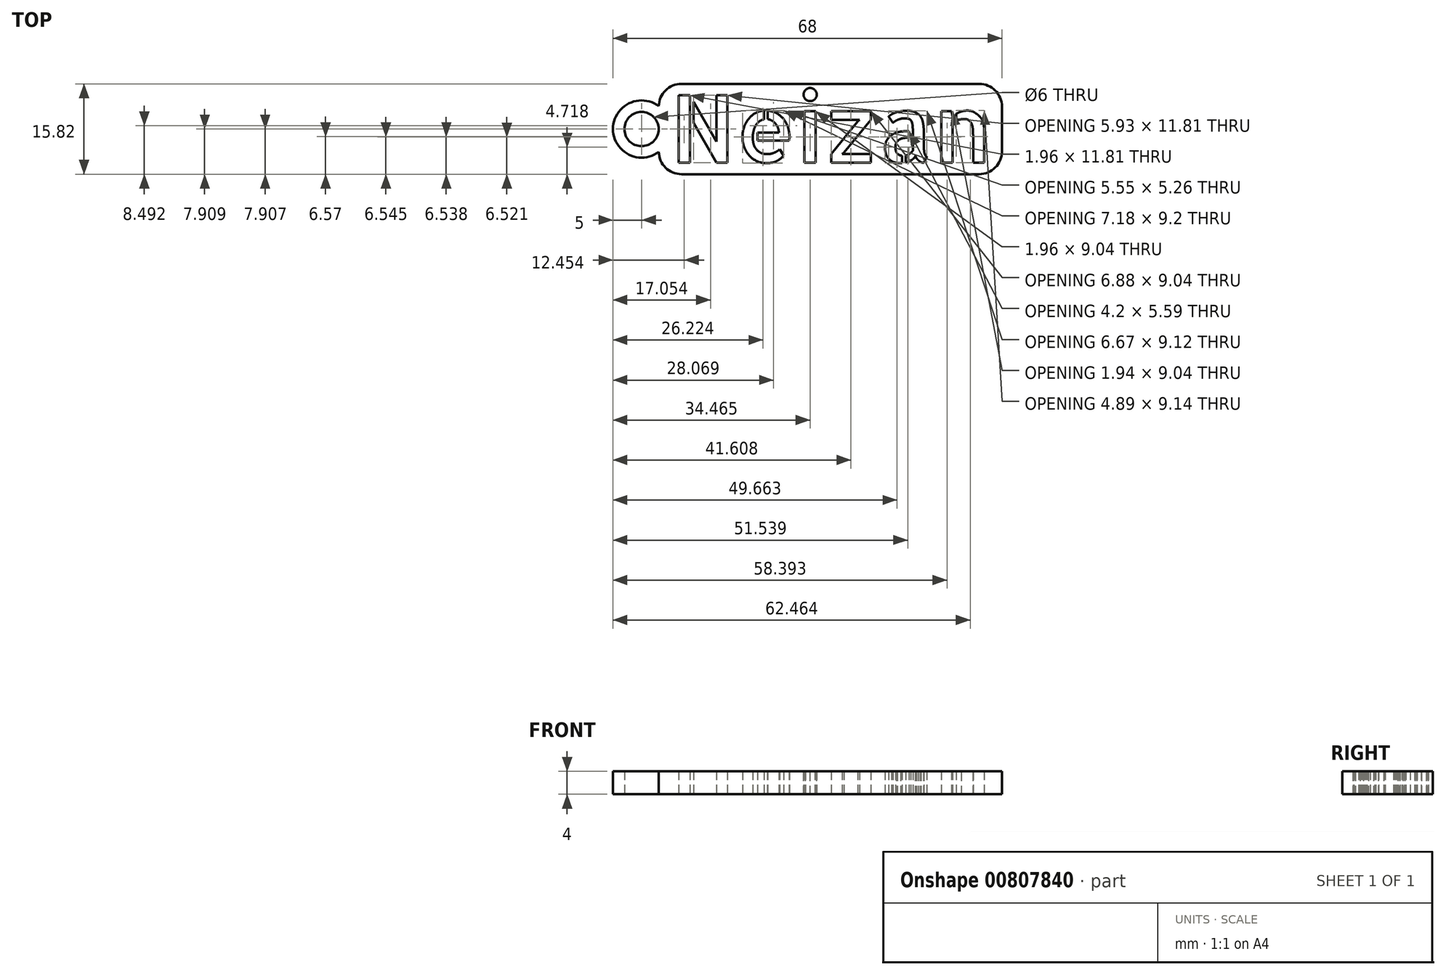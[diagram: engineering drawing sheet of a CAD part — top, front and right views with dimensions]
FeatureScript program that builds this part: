
annotation { "Feature Type Name" : "Feature", "Feature Type Description" : "" }
export const myFeature = defineFeature(function(context is Context, id is Id, definition is map)
    precondition{}
    {
        {
            var Q0;
            Q0=qCreatedBy(makeId("Top.planeOp"),FACE);
            var sketch = newSketch(context, id + "F0", { "sketchPlane" : qUnion([Q0])});
            skLineSegment(sketch, "E0.bottom", {"start": v(-2, -2) * mm, "end": v(58, -2) * mm});
            skLineSegment(sketch, "E0.top", {"start": v(-2, 13.82) * mm, "end": v(58, 13.82) * mm});
            skLineSegment(sketch, "E0.left", {"start": v(-2, -2) * mm, "end": v(-2, 1.9) * mm});
            skLineSegment(sketch, "E0.right", {"start": v(58, -2) * mm, "end": v(58, 13.82) * mm});
            skArc(sketch, "E1", {"start": v(-2, 9.9) * mm, "mid": v(-10, 5.9) * mm, "end": v(-2, 1.9) * mm});
            skLineSegment(sketch, "E2.trimOffspring", {"start": v(-2, 9.9) * mm, "end": v(-2, 13.82) * mm});
            skCircle(sketch, "E3", {"center": v(-5, 5.9) * mm, "radius": 3 * mm});
            skLineSegment(sketch, "E4", {"start": v(58, 5.9) * mm, "end": v(-10, 5.9) * mm, "construction": true});
            skText(sketch, "E5", { "text": "Neizan", "fontName": "AllertaStencil-Regular.ttf"});
            const initialGuessF0  = {"E5": [0, 0, 1, 0, 0.01182]};
            skSetInitialGuess(sketch, initialGuessF0);
            skSolve(sketch);
        }
        {
            var Q0;
            Q0=makeQuery(id+"F0.imprint","IMPRINT",FACE,{"disambiguationData":[TD([[makeQuery(id+"F0.imprint","IMPRINT",EDGE,{"derivedFrom":sQuery(id+"F0.wireOp",EDGE,"E0.bottom")}),1.0]])]});
            extrude(context, id + "F1", {"entities" : qUnion([Q0]), "depth" : 4 * mm, "offsetDistance" : 25 * mm});
        }
        {
            var Q0;
            Q0=makeQuery(id+"F1.opExtrude","SWEPT_EDGE",EDGE,{"disambiguationData":[OSD([sQuery(id+"F0.wireOp",EDGE,"E0.bottom"),sQuery(id+"F0.wireOp",EDGE,"E0.left")])]});
            var Q1;
            Q1=makeQuery(id+"F1.opExtrude","SWEPT_EDGE",EDGE,{"disambiguationData":[OSD([sQuery(id+"F0.wireOp",EDGE,"E0.bottom"),sQuery(id+"F0.wireOp",EDGE,"E0.right")])]});
            var Q2;
            Q2=makeQuery(id+"F1.opExtrude","SWEPT_EDGE",EDGE,{"disambiguationData":[OSD([sQuery(id+"F0.wireOp",EDGE,"E0.top"),sQuery(id+"F0.wireOp",EDGE,"E0.right")])]});
            var Q3;
            Q3=makeQuery(id+"F1.opExtrude","SWEPT_EDGE",EDGE,{"disambiguationData":[OSD([sQuery(id+"F0.wireOp",EDGE,"E0.top"),sQuery(id+"F0.wireOp",EDGE,"E2.trimOffspring")])]});
            fillet(context, id + "F2", {"entities" : qUnion([Q0, Q1, Q2, Q3]), "radius" : 4 * mm, "tangentPropagation" : true, "allowEdgeOverflow" : false});
        }
    });
